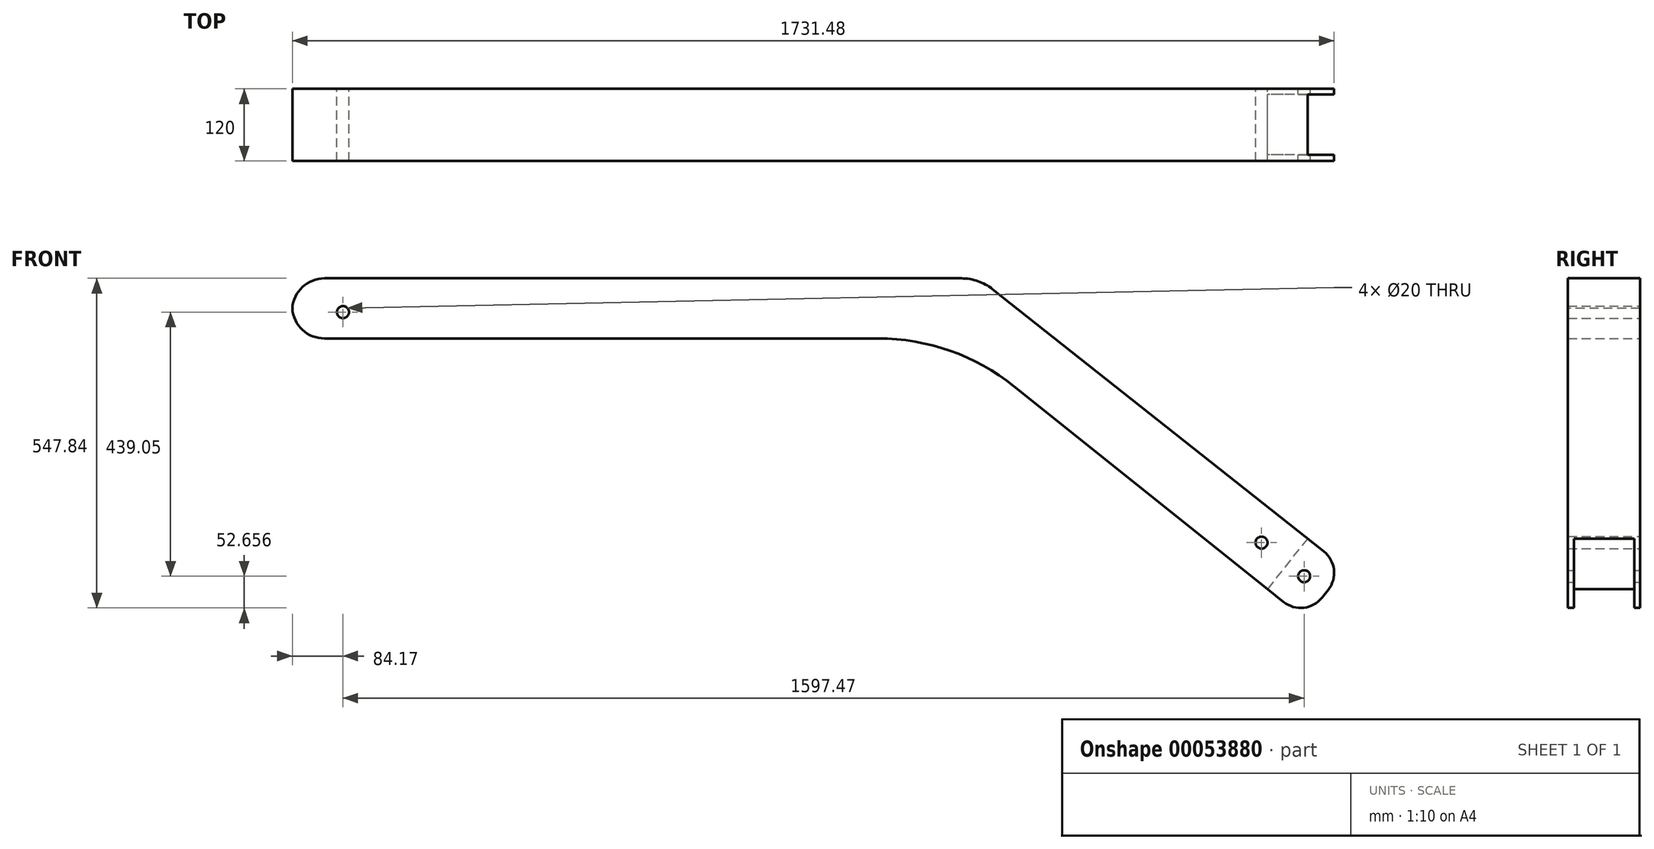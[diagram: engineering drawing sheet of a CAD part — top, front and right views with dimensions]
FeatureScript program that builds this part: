
annotation { "Feature Type Name" : "Feature", "Feature Type Description" : "" }
export const myFeature = defineFeature(function(context is Context, id is Id, definition is map)
    precondition{}
    {
        {
            var Q0;
            Q0=qCreatedBy(makeId("Front.planeOp"),FACE);
            var sketch = newSketch(context, id + "F0", { "sketchPlane" : qUnion([Q0])});
            skLineSegment(sketch, "E0.bottom", {"start": v(-900.62, 159.65) * mm, "end": v(240.64, 159.65) * mm});
            skLineSegment(sketch, "E0.top", {"start": v(-900.62, 59.65) * mm, "end": v(200.02, 59.65) * mm});
            skLineSegment(sketch, "E0.left", {"start": v(-900.62, 159.65) * mm, "end": v(-900.62, 59.65) * mm});
            skLineSegment(sketch, "E1", {"start": v(240.64, 159.65) * mm, "end": v(200.02, 59.65) * mm});
            skLineSegment(sketch, "E2", {"start": v(240.64, 159.65) * mm, "end": v(786.76, -272.83) * mm});
            skLineSegment(sketch, "E3", {"start": v(786.76, -272.83) * mm, "end": v(720.09, -357.02) * mm});
            skLineSegment(sketch, "E4", {"start": v(720.09, -357.02) * mm, "end": v(200.02, 59.65) * mm});
            skCircle(sketch, "E5", {"center": v(710.36, -279.63) * mm, "radius": 10 * mm});
            skCircle(sketch, "E6", {"center": v(-816.33, 103.52) * mm, "radius": 10 * mm});
            skSolve(sketch);
        }
        {
            var Q0;
            Q0=makeQuery(id+"F0.imprint","IMPRINT",FACE,{"disambiguationData":[TD([[makeQuery(id+"F0.imprint","IMPRINT",EDGE,{"derivedFrom":sQuery(id+"F0.wireOp",EDGE,"E0.bottom")}),-1.0]])]});
            var Q1;
            Q1=makeQuery(id+"F0.imprint","IMPRINT",FACE,{"disambiguationData":[TD([[makeQuery(id+"F0.imprint","IMPRINT",EDGE,{"derivedFrom":sQuery(id+"F0.wireOp",EDGE,"E1")}),1.0]])]});
            extrude(context, id + "F1", {"entities" : qUnion([Q0, Q1]), "depth" : 120 * mm});
        }
        {
            var Q0;
            Q0=makeQuery(id+"F1.opExtrude","SWEPT_EDGE",EDGE,{"disambiguationData":[OSD([sQuery(id+"F0.wireOp",EDGE,"E0.bottom"),sQuery(id+"F0.wireOp",EDGE,"E0.left")])]});
            var Q1;
            Q1=makeQuery(id+"F1.opExtrude","SWEPT_EDGE",EDGE,{"disambiguationData":[OSD([sQuery(id+"F0.wireOp",EDGE,"E0.top"),sQuery(id+"F0.wireOp",EDGE,"E0.left")])]});
            fillet(context, id + "F2", {"entities" : qUnion([Q0, Q1]), "radius" : 53.62 * mm, "tangentPropagation" : true, "allowEdgeOverflow" : false});
        }
        {
            var Q0;
            Q0=makeQuery(id+"F1.opExtrude","SWEPT_EDGE",EDGE,{"disambiguationData":[OSD([sQuery(id+"F0.wireOp",EDGE,"E0.bottom"),sQuery(id+"F0.wireOp",EDGE,"E1"),sQuery(id+"F0.wireOp",EDGE,"E2")])]});
            fillet(context, id + "F3", {"entities" : qUnion([Q0]), "radius" : 83.4 * mm, "tangentPropagation" : true, "allowEdgeOverflow" : false});
        }
        {
            var Q0;
            Q0=makeQuery(id+"F1.opExtrude","SWEPT_EDGE",EDGE,{"disambiguationData":[OSD([sQuery(id+"F0.wireOp",EDGE,"E0.top"),sQuery(id+"F0.wireOp",EDGE,"E1"),sQuery(id+"F0.wireOp",EDGE,"E4")])]});
            fillet(context, id + "F4", {"entities" : qUnion([Q0]), "radius" : 360.6 * mm, "tangentPropagation" : true, "allowEdgeOverflow" : false});
        }
        {
            var Q0;
            Q0=makeQuery(id+"F1.opExtrude","SWEPT_FACE",FACE,{"disambiguationData":[OSD([sQuery(id+"F0.wireOp",EDGE,"E3")])]});
            var sketch = newSketch(context, id + "F5", { "sketchPlane" : qUnion([Q0])});
            skLineSegment(sketch, "E7.bottom", {"start": v(-109.57, 275.46) * mm, "end": v(-9.57, 275.46) * mm});
            skLineSegment(sketch, "E7.top", {"start": v(-109.57, 165.46) * mm, "end": v(-9.57, 165.46) * mm});
            skLineSegment(sketch, "E7.left", {"start": v(-109.57, 275.46) * mm, "end": v(-109.57, 165.46) * mm});
            skLineSegment(sketch, "E7.right", {"start": v(-9.57, 275.46) * mm, "end": v(-9.57, 165.46) * mm});
            skSolve(sketch);
        }
        {
            var Q0;
            Q0=makeQuery(id+"F5.imprint","IMPRINT",FACE,{"disambiguationData":[TD([[makeQuery(id+"F5.imprint","IMPRINT",EDGE,{"derivedFrom":sQuery(id+"F5.wireOp",EDGE,"E7.bottom")}),1.0]])]});
            var Q1;
            {var subQ1=sQuery(id+"F0.wireOp",EDGE,"E3");var subQ6=makeQuery(id+"F1.opExtrude","CAP_EDGE",EDGE,{"disambiguationData":[OSD([subQ1])],"isStart":true});Q1=makeQuery(id+"F5.imprint","IMPRINT",FACE,{"disambiguationData":[TD([[makeQuery(id+"F5.imprint","IMPRINT",EDGE,{"derivedFrom":subQ6}),-1.0]])]});}
            var Q2;
            {var subQ1=sQuery(id+"F0.wireOp",EDGE,"E3");var subQ6=makeQuery(id+"F1.opExtrude","CAP_EDGE",EDGE,{"disambiguationData":[OSD([subQ1])],"isStart":false});Q2=makeQuery(id+"F5.imprint","IMPRINT",FACE,{"disambiguationData":[TD([[makeQuery(id+"F5.imprint","IMPRINT",EDGE,{"derivedFrom":subQ6}),1.0]])]});}
            extrude(context, id + "F6", {"entities" : qUnion([Q0, Q1, Q2]), "operationType" : NewBodyOperationType.ADD, "depth" : 80 * mm});
        }
        {
            var Q0;
            Q0=makeQuery(id+"F6.opExtrude","CAP_EDGE",EDGE,{"disambiguationData":[OSD([sQuery(id+"F0.wireOp",EDGE,"E2"),sQuery(id+"F0.wireOp",EDGE,"E3")])],"isStart":false});
            var Q1;
            Q1=makeQuery(id+"F6.opExtrude","CAP_EDGE",EDGE,{"disambiguationData":[OSD([sQuery(id+"F0.wireOp",EDGE,"E3"),sQuery(id+"F0.wireOp",EDGE,"E4")])],"isStart":false});
            fillet(context, id + "F7", {"entities" : qUnion([Q0, Q1]), "radius" : 45.68 * mm, "tangentPropagation" : true, "allowEdgeOverflow" : false});
        }
        {
            var Q0;
            {var subQ0=sQuery(id+"F0.wireOp",EDGE,"E3");Q0=makeQuery(id+"F6.boolean.opBoolean","MERGE",FACE,{"derivedFrom":[makeQuery(id+"F1.opExtrude","CAP_FACE",FACE,{"disambiguationData":[OSD([sQuery(id+"F0.wireOp",EDGE,"E0.bottom"),sQuery(id+"F0.wireOp",EDGE,"E0.top"),sQuery(id+"F0.wireOp",EDGE,"E0.left"),sQuery(id+"F0.wireOp",EDGE,"E2"),subQ0,sQuery(id+"F0.wireOp",EDGE,"E4"),sQuery(id+"F0.wireOp",EDGE,"E5"),sQuery(id+"F0.wireOp",EDGE,"E6")])],"isStart":true}),makeQuery(id+"F6.opExtrude","SWEPT_FACE",FACE,{"disambiguationData":[OSD([subQ0]),TDD([makeQuery(id+"F5.imprint","IMPRINT",EDGE,{"derivedFrom":makeQuery(id+"F1.opExtrude","CAP_EDGE",EDGE,{"disambiguationData":[OSD([subQ0])],"isStart":true})})])]})]});}
            var sketch = newSketch(context, id + "F8", { "sketchPlane" : qUnion([Q0])});
            skCircle(sketch, "E8", {"center": v(-781.14, -335.53) * mm, "radius": 8.6 * mm});
            skCircle(sketch, "E9", {"center": v(-781.14, -335.53) * mm, "radius": 8.7 * mm});
            skSolve(sketch);
        }
        {
            var Q0;
            Q0=sQuery(id+"F8.wireOp",VERTEX,"E8.center");
            var Q1;
            Q1=makeQuery(id+"F1.opExtrude","SWEPT_BODY",BODY,{"disambiguationData":[OSD([sQuery(id+"F0.wireOp",EDGE,"E0.bottom"),sQuery(id+"F0.wireOp",EDGE,"E0.top"),sQuery(id+"F0.wireOp",EDGE,"E0.left"),sQuery(id+"F0.wireOp",EDGE,"E2"),sQuery(id+"F0.wireOp",EDGE,"E3"),sQuery(id+"F0.wireOp",EDGE,"E4"),sQuery(id+"F0.wireOp",EDGE,"E5"),sQuery(id+"F0.wireOp",EDGE,"E6")])]});
            hole(context, id + "F9", {"style" : HoleStyle.SIMPLE, "holeDiameter" : 20 * mm, "endStyle" : HoleEndStyle.THROUGH, "locations" : qUnion([Q0]), "scope" : qUnion([Q1])});
        }
    });
